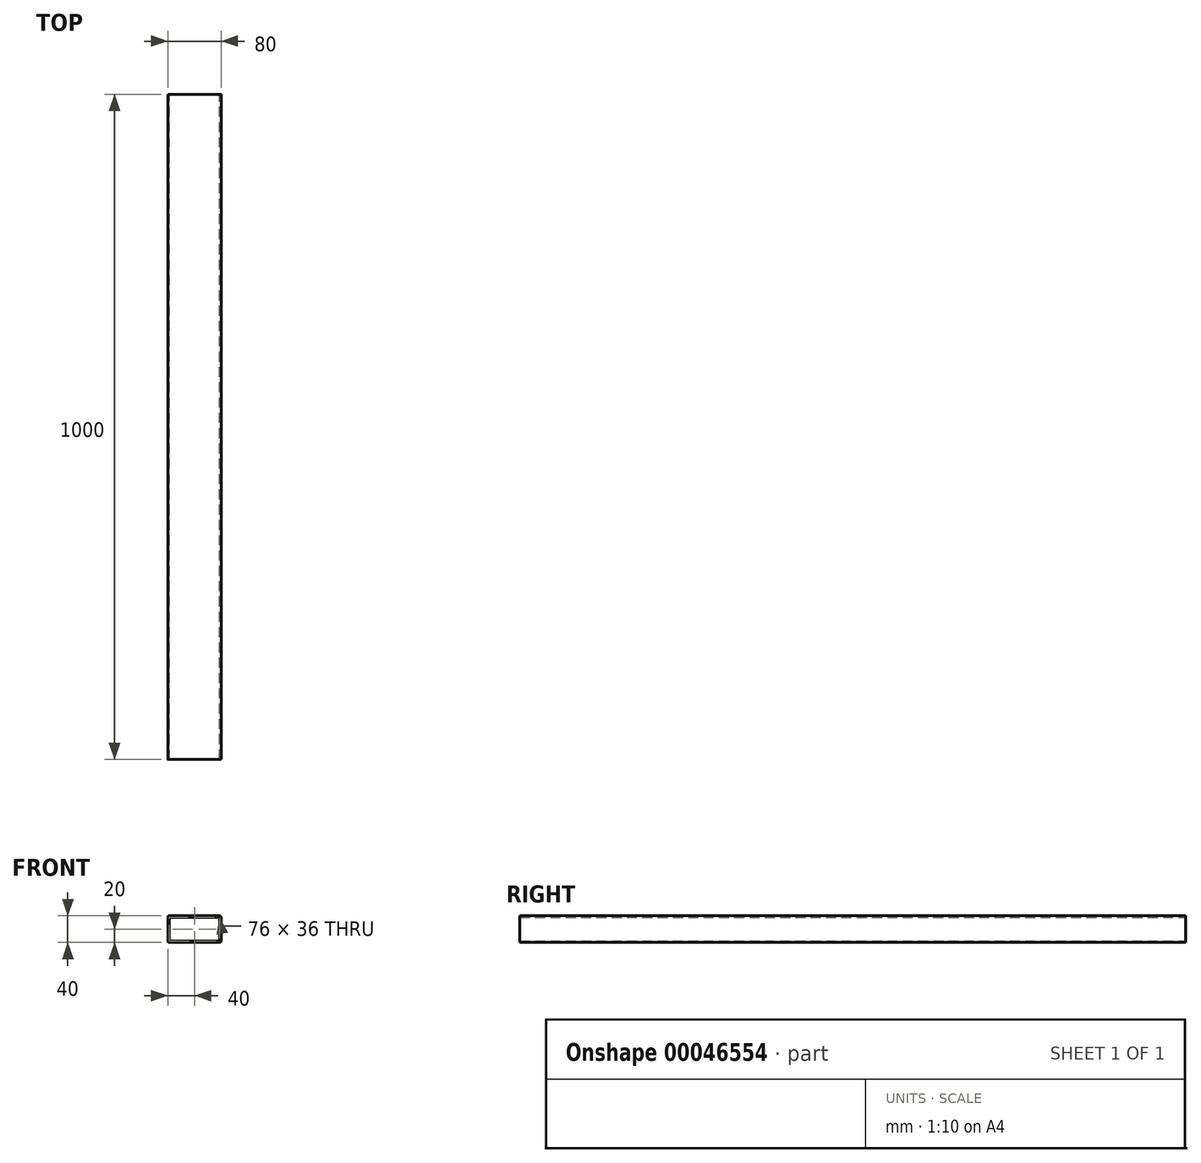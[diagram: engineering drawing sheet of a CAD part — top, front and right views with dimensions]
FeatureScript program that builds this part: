
annotation { "Feature Type Name" : "Feature", "Feature Type Description" : "" }
export const myFeature = defineFeature(function(context is Context, id is Id, definition is map)
    precondition{}
    {
        {
            var Q0;
            Q0=qCreatedBy(makeId("Front.planeOp"),FACE);
            var sketch = newSketch(context, id + "F0", { "sketchPlane" : qUnion([Q0])});
            skLineSegment(sketch, "E0", {"start": v(38, 18) * mm, "end": v(38, -18) * mm});
            skLineSegment(sketch, "E1", {"start": v(-38, 18) * mm, "end": v(38, 18) * mm});
            skLineSegment(sketch, "E2", {"start": v(-38, -18) * mm, "end": v(-38, 18) * mm});
            skLineSegment(sketch, "E3", {"start": v(38, -18) * mm, "end": v(-38, -18) * mm});
            skLineSegment(sketch, "E4", {"start": v(-40, 18) * mm, "end": v(-40, -18) * mm});
            skArc(sketch, "E5", {"start": v(-38, 20) * mm, "mid": v(-39.41, 19.41) * mm, "end": v(-40, 18) * mm});
            skLineSegment(sketch, "E6", {"start": v(38, 20) * mm, "end": v(-38, 20) * mm});
            skArc(sketch, "E7", {"start": v(40, 18) * mm, "mid": v(39.41, 19.41) * mm, "end": v(38, 20) * mm});
            skLineSegment(sketch, "E8", {"start": v(40, -18) * mm, "end": v(40, 18) * mm});
            skArc(sketch, "E9", {"start": v(38, -20) * mm, "mid": v(39.41, -19.41) * mm, "end": v(40, -18) * mm});
            skLineSegment(sketch, "E10", {"start": v(-38, -20) * mm, "end": v(38, -20) * mm});
            skArc(sketch, "E11", {"start": v(-40, -18) * mm, "mid": v(-39.41, -19.41) * mm, "end": v(-38, -20) * mm});
            skSolve(sketch);
        }
        {
            var Q0;
            Q0 = qSketchRegion(id + "F0", true);
            extrude(context, id + "F1", {"entities" : qUnion([Q0]), "depth" : 1000 * mm});
        }
    });
